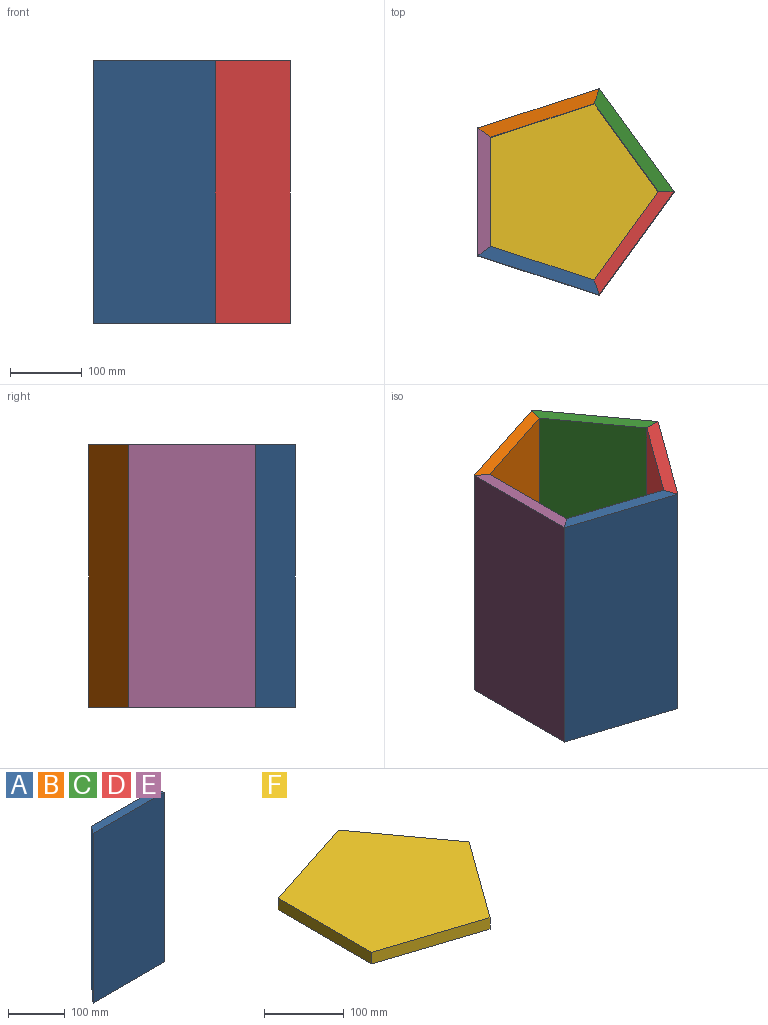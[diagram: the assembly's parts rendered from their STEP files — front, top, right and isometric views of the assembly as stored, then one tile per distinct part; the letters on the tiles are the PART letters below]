
ASSEMBLY  parts=6 mates=5
PART A: 8 faces, bbox 177.8x17.8x365.8 mm
  f0: plane 177.8x17.78mm, normal (0,0,1), area 2931.6mm2, adj f1,f5,f6,f7
  f1: plane 347.98x151.96mm, normal (0,1,0), area 52880.5mm2, adj f0,f3,f6,f7
  f2: plane 177.8x7.62mm, normal (0,0,-1), area 1312.6mm2, adj f4,f5,f6,f7
  f3: plane 166.73x10.16mm, normal (0,0,-1), area 1619mm2, adj f1,f4,f6,f7
  f4: plane 166.73x17.78mm, normal (0,1,0), area 2964.4mm2, adj f2,f3,f6,f7
  f5: plane 365.76x177.8mm, normal (0,-1,0), area 65032.1mm2, adj f0,f2,f6,f7
  f6: plane 365.76x17.78mm, normal (0.81,0.59,0), area 7815.1mm2, adj f0,f1,f2,f3,f4,f5
  f7: plane 365.76x17.78mm, normal (-0.81,0.59,0), area 7815.1mm2, adj f0,f1,f2,f3,f4,f5
PART B: same geometry as A
PART C: same geometry as A
PART D: same geometry as A
PART E: same geometry as A
PART F: 7 faces, bbox 256.4x269.6x17.8 mm
  f0: plane 158.47x51.49mm, normal (-0.31,-0.95,0), area 2962.6mm2, adj f1,f4,f5,f6
  f1: plane 134.8x97.94mm, normal (0.81,-0.59,0), area 2962.6mm2, adj f0,f2,f5,f6
  f2: plane 134.8x97.94mm, normal (0.81,0.59,0), area 2962.6mm2, adj f1,f3,f5,f6
  f3: plane 158.47x51.49mm, normal (-0.31,0.95,0), area 2962.6mm2, adj f2,f4,f5,f6
  f4: plane 166.62x17.78mm, normal (-1,0,0), area 2962.6mm2, adj f0,f3,f5,f6
  f5: plane 269.6x256.41mm, normal (0,0,1), area 47766.6mm2, adj f0,f1,f2,f3,f4
  f6: plane 269.6x256.41mm, normal (0,0,-1), area 47766.6mm2, adj f0,f1,f2,f3,f4
PLACE A rot(axis=(0,0,-1),18deg) t=(-23.6,-57.85,-537.3)mm
PLACE B rot(axis=(0,0,-1),162deg) t=(-23.6,141.08,-537.3)mm
PLACE C rot(axis=(0,0,1),126deg) t=(93.33,103.09,-537.3)mm
PLACE D rot(axis=(0,0,1),54deg) t=(93.33,-19.86,-537.3)mm
PLACE E rot(axis=(0,0,-1),90deg) t=(-95.86,41.61,-537.3)mm
PLACE F rot(axis=(0,0,-1),72deg) t=(8.7,41.68,-537.3)mm
MATE fastened B.f6 <-> E.f7  axis (-0.59,-0.81,0) through (-104.86,124.13,-349.45)mm
MATE fastened A.f6 <-> D.f7  axis (0.95,0.31,0) through (52.1,-91.91,-349.45)mm
MATE fastened C.f7 <-> D.f6  axis (0,-1,0) through (149.11,41.61,-349.45)mm
MATE fastened B.f4 <-> F.f4  axis (0.31,-0.95,0) through (-26.74,150.74,-528.41)mm
MATE fastened E.f6 <-> A.f7  axis (0.59,-0.81,0) through (-104.86,-40.91,-349.45)mm
